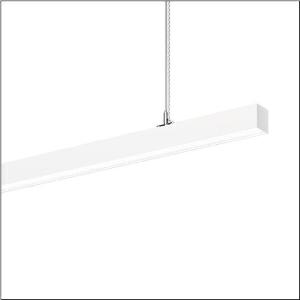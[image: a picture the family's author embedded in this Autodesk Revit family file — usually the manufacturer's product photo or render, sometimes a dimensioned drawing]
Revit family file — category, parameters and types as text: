
# Revit family: silica_r__21_51mx30da34wb_efde
name_source: partatom
category: Lighting Fixtures
units: mm (PartAtom-declared; Revit-internal decimal feet)

## family parameters
Cut with Voids When Loaded = No
Host = Face
Light Source = No
Part Type = Normal
Room Calculation Point = No
Round Connector Dimension = Use Diameter
Shared = No

## types (1)
- --- (1 x LED, 4210 lm, 27.7 W, 3000K)
    Apparent Load = 28 VA
    CIE Flux Codes = 47 79 96 57 100
    Color Rendering = 80
    Color Temperature = 3000K
    Default Elevation = 1800 mm
    Description = Silica® 21, office luminaire, primary optical cover: cover, of PMMA, opal, light emission: direct/indirect distribution, primary light characteristic: symmetric, installation type: suspended mounting, LED, rated luminous flux: 4.210lm, luminous efficacy: 152lm/W, light colour: 830, colour temperature: 3000K, with terminal, 3+2-pole, max. 2.5mm², mains connection: 220..240V, AC, 50/60Hz, rated input power: 27.7W, luminaire housing, of aluminium, traffic white (RAL 9016), length: 1.204mm, width: 53mm, height: 53mm, protection rating (complete): IP20, insulation class (complete): insulation class I (protective earthing), certification: CE, permissible operating ambient temperature: 0..+35°C, standard: EN 50419, packaging unit: 1 piece
    Height = 53 mm
    Lamp = 1 x LED
    Lamp Light Flux = 4210 lm
    Lamp Power = 27.7 W
    Lamp count = 1
    Length = 1204 mm
    Luminous efficacy = 152 lm/W
    Manufacturer = Siteco
    ModVariant = No
    Model = 51MX30DA34WB
    Mounting Place = Ceiling
    Mounting Type = Pendant
    Number of Poles = 1
    OnlyDefault = Yes
    Power Factor = 1
    Product Name = Silica® 21
    Product group = office luminaire | ceiling pendant
    ProductGroupID = 902
    Protection Class = Protection class I
    Protection Degree = IP 20
    RLX_Detail_Level = 1
    RLX_Emergency_Light_Flux = 0 lm
    RLX_Emergency_Type = 0
    RLX_Emergency_Type_DB = No
    RlxData = <blob elided: 21145 chars, md5=87bf4bd2>
    Socket = socket
    Standby Power = 0 W
    System Light Flux = 4210 lm
    System Power = 28 W
    Type Comments = factory setting: luminous flux: 100 % | dim-lin: 254 | 233 mA
    Type Image = l_1297784.jpg
    URL = http://relux.com
    VarID = @adj_047513
    Voltage = 0 V
    Weight = 0.00 kg
    Width = 53 mm

## geometry (parser evidence)
native form markers: Blend x4, Sweep x14
no freeform markers — native parametric forms only
